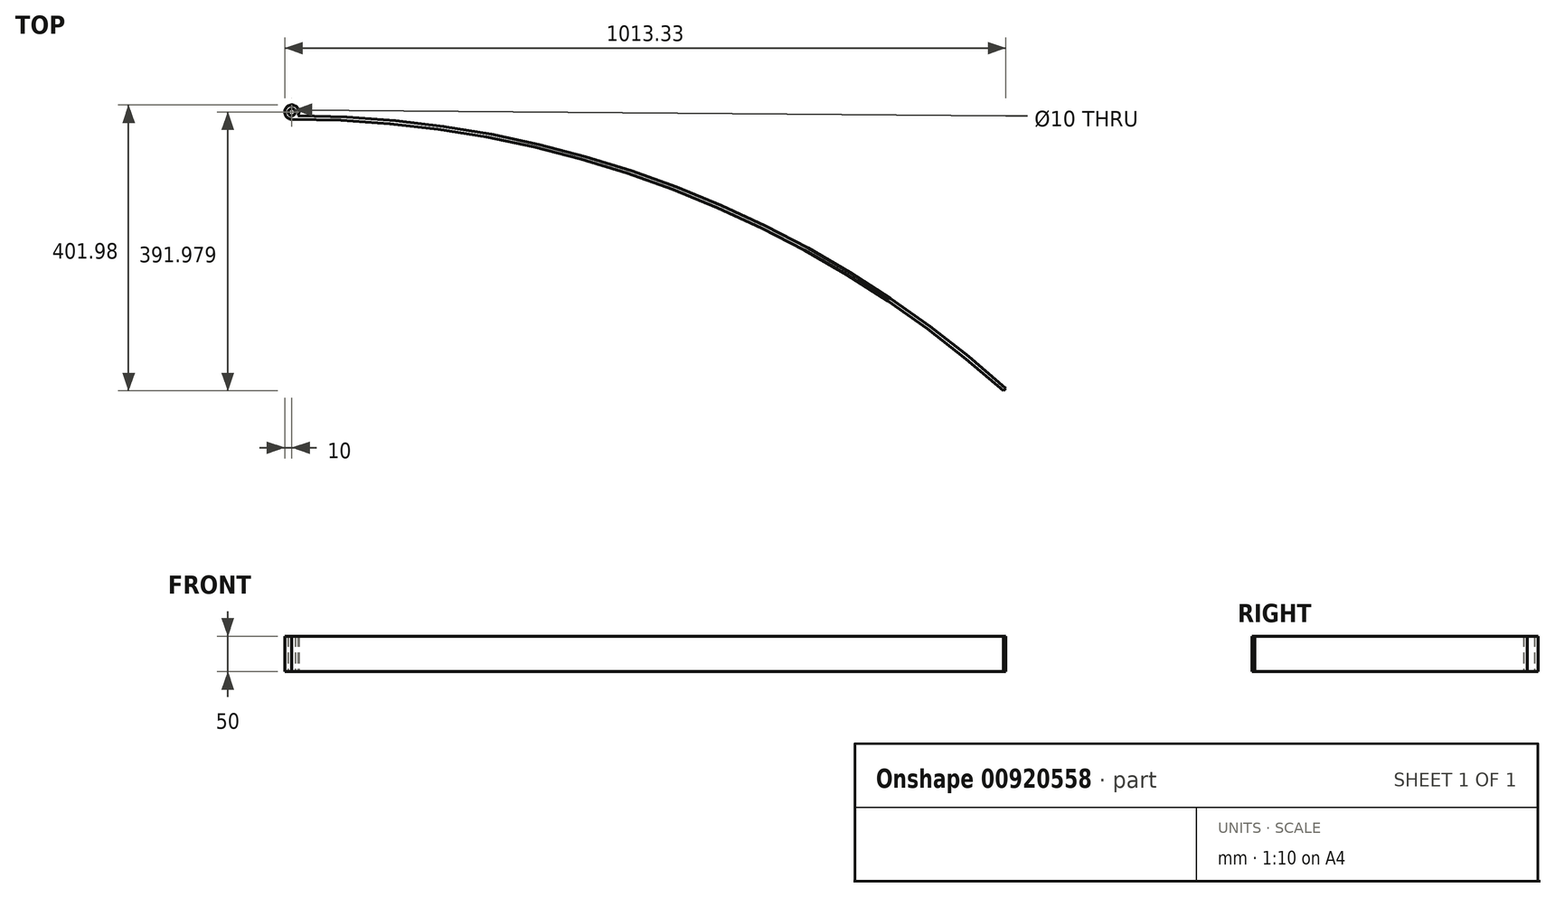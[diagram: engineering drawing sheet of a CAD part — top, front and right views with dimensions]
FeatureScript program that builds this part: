
annotation { "Feature Type Name" : "Feature", "Feature Type Description" : "" }
export const myFeature = defineFeature(function(context is Context, id is Id, definition is map)
    precondition{}
    {
        {
            var Q0;
            Q0=qCreatedBy(makeId("Top.planeOp"),FACE);
            var sketch = newSketch(context, id + "F0", { "sketchPlane" : qUnion([Q0])});
            skArc(sketch, "E0", {"start": v(1000, 1118.03) * mm, "mid": v(535.23, 1401.26) * mm, "end": v(0, 1500) * mm});
            skArc(sketch, "E1.0", {"start": v(1003.33, 1121.76) * mm, "mid": v(537.02, 1405.93) * mm, "end": v(0, 1505) * mm});
            skCircle(sketch, "E2", {"center": v(0, 1510) * mm, "radius": 10 * mm});
            skCircle(sketch, "E3.0", {"center": v(0, 1510) * mm, "radius": 5 * mm});
            skLineSegment(sketch, "E4", {"start": v(0, 1505) * mm, "end": v(0, 1500) * mm});
            skLineSegment(sketch, "E5", {"start": v(1000, 1118.03) * mm, "end": v(1003.33, 1121.76) * mm});
            skSolve(sketch);
        }
        {
            var Q0;
            {var subQ0=sQuery(id+"F0.wireOp",EDGE,"E4");var subQ1=sQuery(id+"F0.wireOp",EDGE,"E1.0");var subQ2=makeQuery(id+"F0.imprint","INTERSECT",VERTEX,{"derivedFrom":[subQ1,subQ0]});Q0=makeQuery(id+"F0.imprint","IMPRINT",FACE,{"disambiguationData":[TD([[makeQuery(id+"F0.imprint","IMPRINT",EDGE,{"disambiguationData":[TD([[subQ2,1.0]])],"derivedFrom":subQ1}),1.0]])]});}
            var Q1;
            Q1=makeQuery(id+"F0.imprint","IMPRINT",FACE,{"disambiguationData":[TD([[makeQuery(id+"F0.imprint","IMPRINT",EDGE,{"derivedFrom":sQuery(id+"F0.wireOp",EDGE,"E3.0")}),-1.0]])]});
            var Q2;
            {var subQ1=sQuery(id+"F0.wireOp",EDGE,"E0");Q2=makeQuery(id+"F0.imprint","IMPRINT",FACE,{"disambiguationData":[TD([[makeQuery(id+"F0.imprint","IMPRINT",EDGE,{"derivedFrom":subQ1}),-1.0]])]});}
            extrude(context, id + "F1", {"entities" : qUnion([Q0, Q1, Q2]), "depth" : 50 * mm, "offsetDistance" : 25 * mm});
        }
    });
